# Revit family: WashbasinUnit-Vitra-EqualSeries-64079+64081+64083
name_source: partatom
category: Furniture Systems
revit_build: Autodesk Revit 2017 (Build: 20160225_1515(x64)
units: mm (PartAtom-declared; Revit-internal decimal feet)

## family parameters
Cut with Voids When Loaded = No
Host = Face
OmniClass Number = 23.40.00.00
OmniClass Title = Equipment and Furnishings
Part Type = Normal
Room Calculation Point = No
Round Connector Dimension = Use Diameter
Shared = Yes

## types (1)
- WashbasinUnit-Vitra-EqualSeries_64079
    Article No. (default) = 64079
    BIMobject category = Bathroom compound units
    Construction Type = Face Mounted
    Default Elevation = 580 mm  [stored 1.90289 ft]
    Depth = 440 mm  [stored 1.44357 ft]
    Description = Equal Washbasin Unit, 40 cm, with Towel Holder
    Design country = Turkey
    Height = 88 mm
    IFC Classification = Furniture
    Manufacturer = Vitra
    Manufacturer name = Vitra
    Masterformat 2014 Code = 13 42 13
    Masterformat 2014 Description = Bathroom Unit Modules
    Model = 64079
    NBS Referans Code = 35-75-08
    NBS Referans Description = Bathroom Cabinets
    Nominal height = 0.000
    Nominal width = 0.000
    OmniClass Code = 23-31 25 13
    OmniClass Description = Bathroom Cabinets
    Primary Material = Vitra-Crome
    Product SKU = 64079
    Product certification = https://vitraglobal.com
    Product data url = https://www.vitraglobal.com
    Product family = Equal
    Product group = Washbasin Unit
    Secondary Material = Vitra-Crome
    Technical description = https://www.vitra.com.tr
    Thrid Material = Vitra-AmericanValnut
    UNSPSC Code = 301815
    UNSPSC Description = Bathroom Cabinets
    URL = https://vitraglobal.com
    Uniclass 1.4 Code = L8241
    Uniclass 1.4 Description = Bathroom Cabinets
    Uniclass 2.0 Code = PR-35-75-08
    Uniclass 2.0 Description = Bathroom Cabinets
    Uniclass 2015 Code = Pr_40_20_93
    Uniclass 2015 Name = Wash basins, sinks and troughs
    Uniformat II Code = E20
    Uniformat II Description = FURNISHINGS
    Warranty Period (Year) = 2
    Weight Net (kg) = 31,200
    Width = 468 mm
    Youtube = https://www.youtube.com

note: [stored X ft] marks values corroborated as IEEE doubles in the binary element streams (Revit-internal decimal feet)

## geometry (parser evidence)
native form markers: Sweep x3
no freeform markers — native parametric forms only
